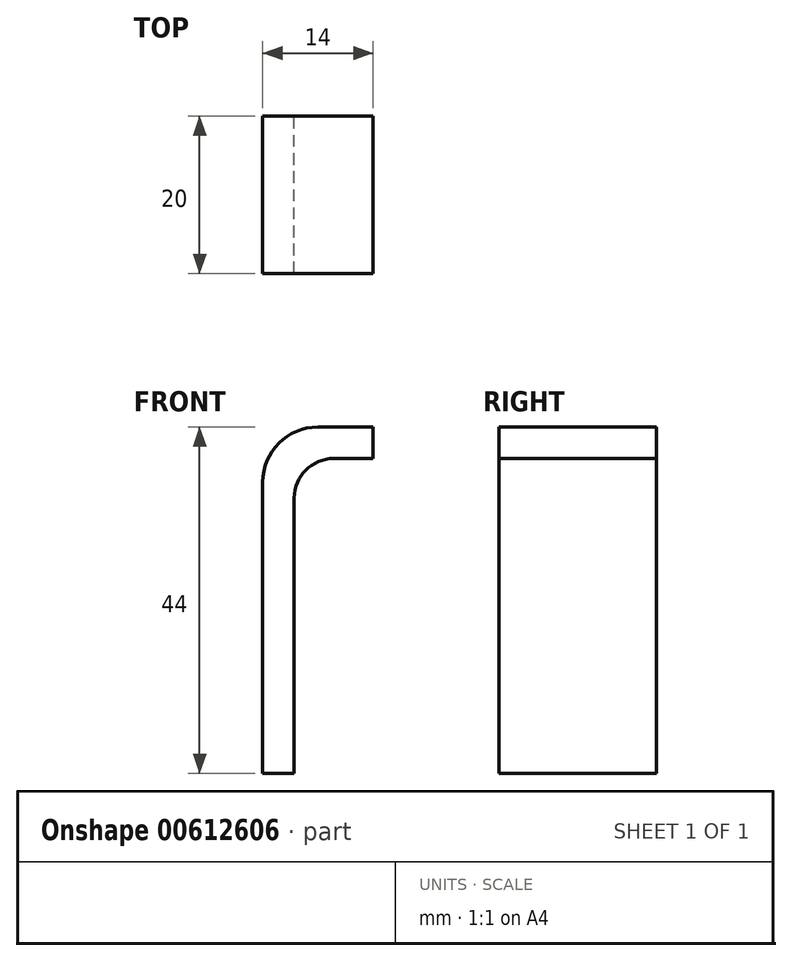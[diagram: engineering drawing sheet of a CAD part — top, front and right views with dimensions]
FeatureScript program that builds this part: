
annotation { "Feature Type Name" : "Feature", "Feature Type Description" : "" }
export const myFeature = defineFeature(function(context is Context, id is Id, definition is map)
    precondition{}
    {
        {
            var Q0;
            Q0=qCreatedBy(makeId("Front.planeOp"),FACE);
            var sketch = newSketch(context, id + "F0", { "sketchPlane" : qUnion([Q0])});
            skLineSegment(sketch, "E0", {"start": v(0, 0) * mm, "end": v(-5, 0) * mm});
            skLineSegment(sketch, "E1", {"start": v(-10, -5) * mm, "end": v(-10, -40) * mm});
            skLineSegment(sketch, "E2.0", {"start": v(-14, -3) * mm, "end": v(-14, -40) * mm});
            skLineSegment(sketch, "E2.1", {"start": v(0, 4) * mm, "end": v(-7, 4) * mm});
            skLineSegment(sketch, "E3", {"start": v(-14, -40) * mm, "end": v(-10, -40) * mm});
            skLineSegment(sketch, "E4", {"start": v(0, 0) * mm, "end": v(0, 4) * mm});
            skPoint(sketch, "E5.visualSharp", {"position": v(-10, 0) * mm});
            skArc(sketch, "E5.filletArc", {"start": v(-5, 0) * mm, "mid": v(-8.54, -1.46) * mm, "end": v(-10, -5) * mm});
            skPoint(sketch, "E6.visualSharp", {"position": v(-14, 4) * mm});
            skArc(sketch, "E6.filletArc", {"start": v(-7, 4) * mm, "mid": v(-11.95, 1.95) * mm, "end": v(-14, -3) * mm});
            skSolve(sketch);
        }
        {
            var Q0;
            Q0=makeQuery(id+"F0.imprint","IMPRINT",FACE,{"disambiguationData":[TD([[makeQuery(id+"F0.imprint","IMPRINT",EDGE,{"derivedFrom":sQuery(id+"F0.wireOp",EDGE,"E0")}),-1.0]])]});
            extrude(context, id + "F1", {"entities" : qUnion([Q0]), "depth" : 20 * mm, "offsetDistance" : 25.4 * mm});
        }
    });
